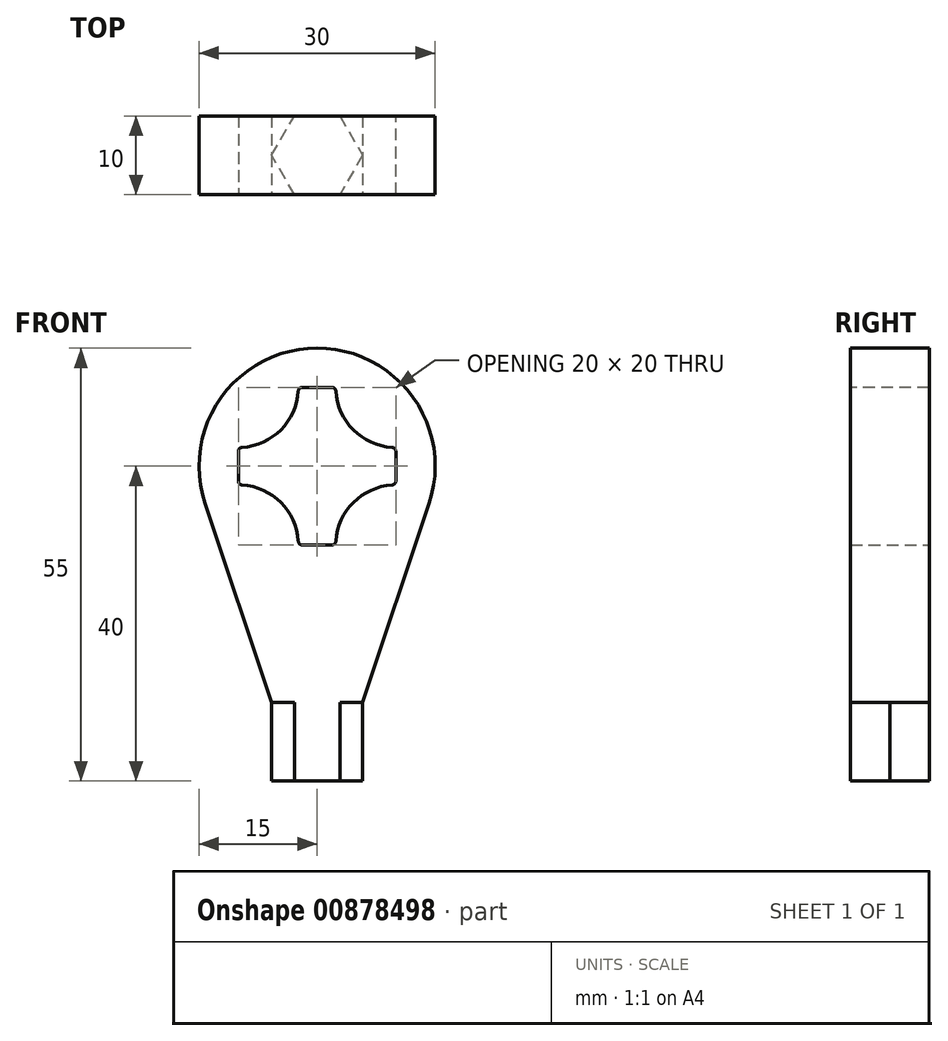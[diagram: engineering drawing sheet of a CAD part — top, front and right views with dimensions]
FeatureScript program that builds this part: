
annotation { "Feature Type Name" : "Feature", "Feature Type Description" : "" }
export const myFeature = defineFeature(function(context is Context, id is Id, definition is map)
    precondition{}
    {
        {
            var Q0;
            Q0=qCreatedBy(makeId("Front.planeOp"),FACE);
            var sketch = newSketch(context, id + "F0", { "sketchPlane" : qUnion([Q0])});
            skLineSegment(sketch, "E0.bottom", {"start": v(10, 10) * mm, "end": v(-10, 10) * mm});
            skLineSegment(sketch, "E0.top", {"start": v(10, -10) * mm, "end": v(-10, -10) * mm});
            skLineSegment(sketch, "E0.left", {"start": v(10, 10) * mm, "end": v(10, -10) * mm});
            skLineSegment(sketch, "E0.right", {"start": v(-10, 10) * mm, "end": v(-10, -10) * mm});
            skPoint(sketch, "E0.middle", {"position": v(0, 0) * mm});
            skCircle(sketch, "E1", {"center": v(0, 0) * mm, "radius": 15 * mm});
            skLineSegment(sketch, "E2", {"start": v(-2.38, 10) * mm, "end": v(2.37, 10) * mm});
            skPoint(sketch, "E3", {"position": v(0, 10) * mm});
            skLineSegment(sketch, "E4", {"start": v(-10, 2.38) * mm, "end": v(-10, -2.38) * mm});
            skLineSegment(sketch, "E5", {"start": v(10, 2.37) * mm, "end": v(10, -2.38) * mm});
            skLineSegment(sketch, "E6", {"start": v(-2.37, -10) * mm, "end": v(2.38, -10) * mm});
            skPoint(sketch, "E7", {"position": v(-10, 0) * mm});
            skPoint(sketch, "E8", {"position": v(10, 0) * mm});
            skPoint(sketch, "E9", {"position": v(0, -10) * mm});
            skCircle(sketch, "E10", {"center": v(-10, 10) * mm, "radius": 7.63 * mm});
            skCircle(sketch, "E11", {"center": v(10, 10) * mm, "radius": 7.63 * mm});
            skCircle(sketch, "E12", {"center": v(10, -10) * mm, "radius": 7.63 * mm});
            skCircle(sketch, "E13", {"center": v(-10, -10) * mm, "radius": 7.63 * mm});
            skSolve(sketch);
        }
        {
            var Q0;
            {var subQ0=sQuery(id+"F0.wireOp",EDGE,"E13");var subQ1=sQuery(id+"F0.wireOp",EDGE,"E0.right");var subQ2=makeQuery(id+"F0.imprint","INTERSECT",VERTEX,{"derivedFrom":[subQ1,subQ0]});Q0=makeQuery(id+"F0.imprint","IMPRINT",FACE,{"disambiguationData":[TD([[makeQuery(id+"F0.imprint","IMPRINT",EDGE,{"disambiguationData":[TD([[subQ2,1.0]])],"derivedFrom":subQ1}),-1.0]])]});}
            var Q1;
            {var subQ1=sQuery(id+"F0.wireOp",EDGE,"E0.bottom");var subQ3=sQuery(id+"F0.wireOp",EDGE,"E10");var subQ5=makeQuery(id+"F0.imprint","INTERSECT",VERTEX,{"derivedFrom":[subQ1,subQ3]});Q1=makeQuery(id+"F0.imprint","IMPRINT",FACE,{"disambiguationData":[TD([[makeQuery(id+"F0.imprint","IMPRINT",EDGE,{"disambiguationData":[TD([[subQ5,-1.0]])],"derivedFrom":subQ1}),-1.0]])]});}
            var Q2;
            {var subQ0=sQuery(id+"F0.wireOp",EDGE,"E10");var subQ1=sQuery(id+"F0.wireOp",EDGE,"E0.bottom");var subQ2=makeQuery(id+"F0.imprint","INTERSECT",VERTEX,{"derivedFrom":[subQ1,subQ0]});Q2=makeQuery(id+"F0.imprint","IMPRINT",FACE,{"disambiguationData":[TD([[makeQuery(id+"F0.imprint","IMPRINT",EDGE,{"disambiguationData":[TD([[subQ2,-1.0]])],"derivedFrom":subQ1}),1.0]])]});}
            var Q3;
            {var subQ0=sQuery(id+"F0.wireOp",EDGE,"E10");var subQ1=sQuery(id+"F0.wireOp",EDGE,"E0.bottom");var subQ2=makeQuery(id+"F0.imprint","INTERSECT",VERTEX,{"derivedFrom":[subQ1,subQ0]});Q3=makeQuery(id+"F0.imprint","IMPRINT",FACE,{"disambiguationData":[TD([[makeQuery(id+"F0.imprint","IMPRINT",EDGE,{"disambiguationData":[TD([[subQ2,1.0]])],"derivedFrom":subQ1}),-1.0]])]});}
            var Q4;
            {var subQ3=sQuery(id+"F0.wireOp",EDGE,"E0.left");var subQ6=sQuery(id+"F0.wireOp",EDGE,"E0.bottom");var subQ7=makeQuery(id+"F0.imprint","INTERSECT",VERTEX,{"derivedFrom":[subQ6,subQ3]});Q4=makeQuery(id+"F0.imprint","IMPRINT",FACE,{"disambiguationData":[TD([[makeQuery(id+"F0.imprint","IMPRINT",EDGE,{"disambiguationData":[TD([[subQ7,-1.0]])],"derivedFrom":subQ6}),-1.0]])]});}
            var Q5;
            {var subQ0=sQuery(id+"F0.wireOp",EDGE,"E12");var subQ1=sQuery(id+"F0.wireOp",EDGE,"E0.left");var subQ2=makeQuery(id+"F0.imprint","INTERSECT",VERTEX,{"derivedFrom":[subQ1,subQ0]});Q5=makeQuery(id+"F0.imprint","IMPRINT",FACE,{"disambiguationData":[TD([[makeQuery(id+"F0.imprint","IMPRINT",EDGE,{"disambiguationData":[TD([[subQ2,1.0]])],"derivedFrom":subQ1}),1.0]])]});}
            var Q6;
            {var subQ1=sQuery(id+"F0.wireOp",EDGE,"E0.left");var subQ6=sQuery(id+"F0.wireOp",EDGE,"E0.top");var subQ7=makeQuery(id+"F0.imprint","INTERSECT",VERTEX,{"derivedFrom":[subQ6,subQ1]});Q6=makeQuery(id+"F0.imprint","IMPRINT",FACE,{"disambiguationData":[TD([[makeQuery(id+"F0.imprint","IMPRINT",EDGE,{"disambiguationData":[TD([[subQ7,-1.0]])],"derivedFrom":subQ6}),1.0]])]});}
            var Q7;
            {var subQ0=sQuery(id+"F0.wireOp",EDGE,"E13");var subQ1=sQuery(id+"F0.wireOp",EDGE,"E0.top");var subQ2=makeQuery(id+"F0.imprint","INTERSECT",VERTEX,{"derivedFrom":[subQ1,subQ0]});Q7=makeQuery(id+"F0.imprint","IMPRINT",FACE,{"disambiguationData":[TD([[makeQuery(id+"F0.imprint","IMPRINT",EDGE,{"disambiguationData":[TD([[subQ2,1.0]])],"derivedFrom":subQ1}),1.0]])]});}
            var Q8;
            {var subQ0=sQuery(id+"F0.wireOp",EDGE,"E13");var subQ1=sQuery(id+"F0.wireOp",EDGE,"E0.top");var subQ2=makeQuery(id+"F0.imprint","INTERSECT",VERTEX,{"derivedFrom":[subQ1,subQ0]});Q8=makeQuery(id+"F0.imprint","IMPRINT",FACE,{"disambiguationData":[TD([[makeQuery(id+"F0.imprint","IMPRINT",EDGE,{"disambiguationData":[TD([[subQ2,-1.0]])],"derivedFrom":subQ1}),1.0]])]});}
            var Q9;
            {var subQ0=sQuery(id+"F0.wireOp",EDGE,"E13");var subQ1=sQuery(id+"F0.wireOp",EDGE,"E0.top");var subQ2=makeQuery(id+"F0.imprint","INTERSECT",VERTEX,{"derivedFrom":[subQ1,subQ0]});Q9=makeQuery(id+"F0.imprint","IMPRINT",FACE,{"disambiguationData":[TD([[makeQuery(id+"F0.imprint","IMPRINT",EDGE,{"disambiguationData":[TD([[subQ2,-1.0]])],"derivedFrom":subQ1}),-1.0]])]});}
            var Q10;
            {var subQ0=sQuery(id+"F0.wireOp",EDGE,"E0.left");var subQ1=sQuery(id+"F0.wireOp",EDGE,"E0.top");var subQ2=makeQuery(id+"F0.imprint","INTERSECT",VERTEX,{"derivedFrom":[subQ1,subQ0]});Q10=makeQuery(id+"F0.imprint","IMPRINT",FACE,{"disambiguationData":[TD([[makeQuery(id+"F0.imprint","IMPRINT",EDGE,{"disambiguationData":[TD([[subQ2,-1.0]])],"derivedFrom":subQ1}),-1.0]])]});}
            var Q11;
            {var subQ0=sQuery(id+"F0.wireOp",EDGE,"E0.left");var subQ1=sQuery(id+"F0.wireOp",EDGE,"E0.bottom");var subQ2=makeQuery(id+"F0.imprint","INTERSECT",VERTEX,{"derivedFrom":[subQ1,subQ0]});Q11=makeQuery(id+"F0.imprint","IMPRINT",FACE,{"disambiguationData":[TD([[makeQuery(id+"F0.imprint","IMPRINT",EDGE,{"disambiguationData":[TD([[subQ2,-1.0]])],"derivedFrom":subQ1}),1.0]])]});}
            extrude(context, id + "F1", {"entities" : qUnion([Q0, Q1, Q2, Q3, Q4, Q5, Q6, Q7, Q8, Q9, Q10, Q11]), "depth" : 3 * mm, "offsetDistance" : 25 * mm});
        }
        {
            var Q0;
            Q0=makeQuery(id+"F1.opExtrude","CAP_FACE",FACE,{"disambiguationData":[OSD([sQuery(id+"F0.wireOp",EDGE,"E0.bottom"),sQuery(id+"F0.wireOp",EDGE,"E0.top"),sQuery(id+"F0.wireOp",EDGE,"E0.left"),sQuery(id+"F0.wireOp",EDGE,"E0.right"),sQuery(id+"F0.wireOp",EDGE,"E1"),sQuery(id+"F0.wireOp",EDGE,"E10"),sQuery(id+"F0.wireOp",EDGE,"E11"),sQuery(id+"F0.wireOp",EDGE,"E12"),sQuery(id+"F0.wireOp",EDGE,"E13")])],"isStart":false});
            var sketch = newSketch(context, id + "F2", { "sketchPlane" : qUnion([Q0])});
            skLineSegment(sketch, "E14", {"start": v(-15, 0) * mm, "end": v(-15, -40) * mm});
            skLineSegment(sketch, "E15", {"start": v(-15, -40) * mm, "end": v(15, -40) * mm});
            skLineSegment(sketch, "E16", {"start": v(15, -40) * mm, "end": v(15, 0) * mm});
            skSolve(sketch);
        }
        {
            var Q0;
            Q0=qCreatedBy(makeId("Top.planeOp"),FACE);
            cPlane(context, id + "F3", {"entities" : qUnion([Q0]), "cplaneType" : CPlaneType.OFFSET, "offset" : 40 * mm, "oppositeDirection" : true, "width" : 150 * mm, "height" : 150 * mm});
        }
        {
            var Q0;
            Q0=qCreatedBy(id+"F3.planeOp",FACE);
            var sketch = newSketch(context, id + "F4", { "sketchPlane" : qUnion([Q0])});
            skLineSegment(sketch, "E17", {"start": v(-15, -1.5) * mm, "end": v(15, -1.5) * mm, "construction": true});
            skCircle(sketch, "E18.cCircle", {"center": v(0, -1.5) * mm, "radius": 5 * mm, "construction": true});
            skLineSegment(sketch, "E18.0", {"start": v(-2.89, 3.5) * mm, "end": v(2.89, 3.5) * mm});
            skLineSegment(sketch, "E18.1", {"start": v(2.89, 3.5) * mm, "end": v(5.77, -1.5) * mm});
            skLineSegment(sketch, "E18.2", {"start": v(5.77, -1.5) * mm, "end": v(2.89, -6.5) * mm});
            skLineSegment(sketch, "E18.3", {"start": v(2.89, -6.5) * mm, "end": v(-2.89, -6.5) * mm});
            skLineSegment(sketch, "E18.4", {"start": v(-2.89, -6.5) * mm, "end": v(-5.77, -1.5) * mm});
            skLineSegment(sketch, "E18.5", {"start": v(-5.77, -1.5) * mm, "end": v(-2.89, 3.5) * mm});
            skPoint(sketch, "E18.0.midPoint", {"position": v(0, 3.5) * mm});
            skLineSegment(sketch, "E19", {"start": v(0, 0) * mm, "end": v(0, -3) * mm});
            skSolve(sketch);
        }
        {
            var Q0;
            Q0=makeQuery(id+"F4.imprint","IMPRINT",FACE,{"disambiguationData":[TD([[makeQuery(id+"F4.imprint","IMPRINT",EDGE,{"derivedFrom":sQuery(id+"F4.wireOp",EDGE,"E18.0")}),-1.0]])]});
            extrude(context, id + "F5", {"entities" : qUnion([Q0]), "depth" : 10 * mm, "offsetDistance" : 25 * mm});
        }
        {
            var Q0;
            Q0=makeQuery(id+"F1.opExtrude","CAP_FACE",FACE,{"disambiguationData":[OSD([sQuery(id+"F0.wireOp",EDGE,"E0.bottom"),sQuery(id+"F0.wireOp",EDGE,"E0.top"),sQuery(id+"F0.wireOp",EDGE,"E0.left"),sQuery(id+"F0.wireOp",EDGE,"E0.right"),sQuery(id+"F0.wireOp",EDGE,"E1"),sQuery(id+"F0.wireOp",EDGE,"E10"),sQuery(id+"F0.wireOp",EDGE,"E11"),sQuery(id+"F0.wireOp",EDGE,"E12"),sQuery(id+"F0.wireOp",EDGE,"E13")])],"isStart":true});
            var sketch = newSketch(context, id + "F6", { "sketchPlane" : qUnion([Q0])});
            skLineSegment(sketch, "E20", {"start": v(-14.22, -4.76) * mm, "end": v(-5.77, -30) * mm});
            skLineSegment(sketch, "E21", {"start": v(-5.77, -30) * mm, "end": v(5.77, -30) * mm});
            skLineSegment(sketch, "E22", {"start": v(5.77, -30) * mm, "end": v(14.22, -4.76) * mm});
            skArc(sketch, "E23.0", {"start": v(-14.22, -4.76) * mm, "mid": v(0, -15) * mm, "end": v(14.22, -4.76) * mm});
            skSolve(sketch);
        }
        {
            var Q0;
            Q0=makeQuery(id+"F6.imprint","IMPRINT",FACE,{"disambiguationData":[TD([[makeQuery(id+"F6.imprint","IMPRINT",EDGE,{"derivedFrom":sQuery(id+"F6.wireOp",EDGE,"E20")}),1.0]])]});
            var Q1;
            Q1=makeQuery(id+"F1.opExtrude","CAP_FACE",FACE,{"disambiguationData":[OSD([sQuery(id+"F0.wireOp",EDGE,"E0.bottom"),sQuery(id+"F0.wireOp",EDGE,"E0.top"),sQuery(id+"F0.wireOp",EDGE,"E0.left"),sQuery(id+"F0.wireOp",EDGE,"E0.right"),sQuery(id+"F0.wireOp",EDGE,"E1"),sQuery(id+"F0.wireOp",EDGE,"E10"),sQuery(id+"F0.wireOp",EDGE,"E11"),sQuery(id+"F0.wireOp",EDGE,"E12"),sQuery(id+"F0.wireOp",EDGE,"E13")])],"isStart":false});
            extrude(context, id + "F7", {"entities" : qUnion([Q0]), "endBound" : BoundingType.UP_TO_SURFACE, "oppositeDirection" : true, "depth" : 25 * mm, "endBoundEntityFace" : qUnion([Q1]), "offsetDistance" : 25 * mm});
        }
        {
            var Q0;
            Q0=makeQuery(id+"F7.opExtrude","CAP_FACE",FACE,{"disambiguationData":[OSD([sQuery(id+"F6.wireOp",EDGE,"E20"),sQuery(id+"F6.wireOp",EDGE,"E21"),sQuery(id+"F6.wireOp",EDGE,"E22"),sQuery(id+"F6.wireOp",EDGE,"E23.0")])],"isStart":true});
            var Q1;
            Q1=makeQuery(id+"F1.opExtrude","CAP_FACE",FACE,{"disambiguationData":[OSD([sQuery(id+"F0.wireOp",EDGE,"E0.bottom"),sQuery(id+"F0.wireOp",EDGE,"E0.top"),sQuery(id+"F0.wireOp",EDGE,"E0.left"),sQuery(id+"F0.wireOp",EDGE,"E0.right"),sQuery(id+"F0.wireOp",EDGE,"E1"),sQuery(id+"F0.wireOp",EDGE,"E10"),sQuery(id+"F0.wireOp",EDGE,"E11"),sQuery(id+"F0.wireOp",EDGE,"E12"),sQuery(id+"F0.wireOp",EDGE,"E13")])],"isStart":true});
            var Q2;
            Q2=makeQuery(id+"F5.opExtrude","SWEPT_FACE",FACE,{"disambiguationData":[OSD([sQuery(id+"F4.wireOp",EDGE,"E18.0")])]});
            extrude(context, id + "F8", {"entities" : qUnion([Q0, Q1]), "endBound" : BoundingType.UP_TO_SURFACE, "depth" : 25 * mm, "endBoundEntityFace" : qUnion([Q2]), "offsetDistance" : 25 * mm});
        }
        {
            var Q0;
            Q0=makeQuery(id+"F1.opExtrude","CAP_FACE",FACE,{"disambiguationData":[OSD([sQuery(id+"F0.wireOp",EDGE,"E0.bottom"),sQuery(id+"F0.wireOp",EDGE,"E0.top"),sQuery(id+"F0.wireOp",EDGE,"E0.left"),sQuery(id+"F0.wireOp",EDGE,"E0.right"),sQuery(id+"F0.wireOp",EDGE,"E1"),sQuery(id+"F0.wireOp",EDGE,"E10"),sQuery(id+"F0.wireOp",EDGE,"E11"),sQuery(id+"F0.wireOp",EDGE,"E12"),sQuery(id+"F0.wireOp",EDGE,"E13")])],"isStart":false});
            var Q1;
            Q1=makeQuery(id+"F7.opExtrude","CAP_FACE",FACE,{"disambiguationData":[OSD([sQuery(id+"F6.wireOp",EDGE,"E20"),sQuery(id+"F6.wireOp",EDGE,"E21"),sQuery(id+"F6.wireOp",EDGE,"E22"),sQuery(id+"F6.wireOp",EDGE,"E23.0")])],"isStart":false});
            var Q2;
            Q2=makeQuery(id+"F5.opExtrude","SWEPT_FACE",FACE,{"disambiguationData":[OSD([sQuery(id+"F4.wireOp",EDGE,"E18.3")])]});
            extrude(context, id + "F9", {"entities" : qUnion([Q0, Q1]), "endBound" : BoundingType.UP_TO_SURFACE, "depth" : 25 * mm, "endBoundEntityFace" : qUnion([Q2]), "offsetDistance" : 25 * mm});
        }
        {
            var Q0;
            Q0=makeQuery(id+"F5.opExtrude","SWEPT_BODY",BODY,{"disambiguationData":[OSD([sQuery(id+"F4.wireOp",EDGE,"E18.0"),sQuery(id+"F4.wireOp",EDGE,"E18.1"),sQuery(id+"F4.wireOp",EDGE,"E18.2"),sQuery(id+"F4.wireOp",EDGE,"E18.3"),sQuery(id+"F4.wireOp",EDGE,"E18.4"),sQuery(id+"F4.wireOp",EDGE,"E18.5")])]});
            var Q1;
            Q1=makeQuery(id+"F8.opExtrude","SWEPT_BODY",BODY,{"disambiguationData":[OSD([sQuery(id+"F6.wireOp",EDGE,"E20"),sQuery(id+"F6.wireOp",EDGE,"E21"),sQuery(id+"F6.wireOp",EDGE,"E22"),sQuery(id+"F6.wireOp",EDGE,"E23.0")])]});
            var Q2;
            Q2=makeQuery(id+"F7.opExtrude","SWEPT_BODY",BODY,{"disambiguationData":[OSD([sQuery(id+"F6.wireOp",EDGE,"E20"),sQuery(id+"F6.wireOp",EDGE,"E21"),sQuery(id+"F6.wireOp",EDGE,"E22"),sQuery(id+"F6.wireOp",EDGE,"E23.0")])]});
            var Q3;
            Q3=makeQuery(id+"F9.opExtrude","SWEPT_BODY",BODY,{"disambiguationData":[OSD([sQuery(id+"F6.wireOp",EDGE,"E20"),sQuery(id+"F6.wireOp",EDGE,"E21"),sQuery(id+"F6.wireOp",EDGE,"E22"),sQuery(id+"F6.wireOp",EDGE,"E23.0")])]});
            var Q4;
            Q4=makeQuery(id+"F8.opExtrude","SWEPT_BODY",BODY,{"disambiguationData":[OSD([sQuery(id+"F0.wireOp",EDGE,"E0.bottom"),sQuery(id+"F0.wireOp",EDGE,"E0.top"),sQuery(id+"F0.wireOp",EDGE,"E0.left"),sQuery(id+"F0.wireOp",EDGE,"E0.right"),sQuery(id+"F0.wireOp",EDGE,"E1"),sQuery(id+"F0.wireOp",EDGE,"E10"),sQuery(id+"F0.wireOp",EDGE,"E11"),sQuery(id+"F0.wireOp",EDGE,"E12"),sQuery(id+"F0.wireOp",EDGE,"E13")])]});
            var Q5;
            Q5=makeQuery(id+"F1.opExtrude","SWEPT_BODY",BODY,{"disambiguationData":[OSD([sQuery(id+"F0.wireOp",EDGE,"E0.bottom"),sQuery(id+"F0.wireOp",EDGE,"E0.top"),sQuery(id+"F0.wireOp",EDGE,"E0.left"),sQuery(id+"F0.wireOp",EDGE,"E0.right"),sQuery(id+"F0.wireOp",EDGE,"E1"),sQuery(id+"F0.wireOp",EDGE,"E10"),sQuery(id+"F0.wireOp",EDGE,"E11"),sQuery(id+"F0.wireOp",EDGE,"E12"),sQuery(id+"F0.wireOp",EDGE,"E13")])]});
            var Q6;
            Q6=makeQuery(id+"F9.opExtrude","SWEPT_BODY",BODY,{"disambiguationData":[OSD([sQuery(id+"F0.wireOp",EDGE,"E0.bottom"),sQuery(id+"F0.wireOp",EDGE,"E0.top"),sQuery(id+"F0.wireOp",EDGE,"E0.left"),sQuery(id+"F0.wireOp",EDGE,"E0.right"),sQuery(id+"F0.wireOp",EDGE,"E1"),sQuery(id+"F0.wireOp",EDGE,"E10"),sQuery(id+"F0.wireOp",EDGE,"E11"),sQuery(id+"F0.wireOp",EDGE,"E12"),sQuery(id+"F0.wireOp",EDGE,"E13")])]});
            booleanBodies(context, id + "F10", {"operationType" : BooleanOperationType.UNION, "tools" : qUnion([Q0, Q1, Q2, Q3, Q4, Q5, Q6])});
        }
        {
            var Q0;
            {var subQ0=sQuery(id+"F0.wireOp",EDGE,"E12");var subQ1=sQuery(id+"F0.wireOp",EDGE,"E0.left");Q0=makeQuery(id+"F10.opBoolean","MERGE",EDGE,{"derivedFrom":[makeQuery(id+"F1.opExtrude","SWEPT_EDGE",EDGE,{"disambiguationData":[OSD([subQ1,subQ0])]}),makeQuery(id+"F8.opExtrude","SWEPT_EDGE",EDGE,{"disambiguationData":[OSD([subQ1,subQ0])]}),makeQuery(id+"F9.opExtrude","SWEPT_EDGE",EDGE,{"disambiguationData":[OSD([subQ1,subQ0])]})]});}
            var Q1;
            {var subQ0=sQuery(id+"F0.wireOp",EDGE,"E11");var subQ1=sQuery(id+"F0.wireOp",EDGE,"E0.left");Q1=makeQuery(id+"F10.opBoolean","MERGE",EDGE,{"derivedFrom":[makeQuery(id+"F1.opExtrude","SWEPT_EDGE",EDGE,{"disambiguationData":[OSD([subQ1,subQ0])]}),makeQuery(id+"F8.opExtrude","SWEPT_EDGE",EDGE,{"disambiguationData":[OSD([subQ1,subQ0])]}),makeQuery(id+"F9.opExtrude","SWEPT_EDGE",EDGE,{"disambiguationData":[OSD([subQ1,subQ0])]})]});}
            var Q2;
            {var subQ0=sQuery(id+"F0.wireOp",EDGE,"E12");var subQ1=sQuery(id+"F0.wireOp",EDGE,"E0.top");Q2=makeQuery(id+"F10.opBoolean","MERGE",EDGE,{"derivedFrom":[makeQuery(id+"F1.opExtrude","SWEPT_EDGE",EDGE,{"disambiguationData":[OSD([subQ1,subQ0])]}),makeQuery(id+"F8.opExtrude","SWEPT_EDGE",EDGE,{"disambiguationData":[OSD([subQ1,subQ0])]}),makeQuery(id+"F9.opExtrude","SWEPT_EDGE",EDGE,{"disambiguationData":[OSD([subQ1,subQ0])]})]});}
            var Q3;
            {var subQ0=sQuery(id+"F0.wireOp",EDGE,"E13");var subQ1=sQuery(id+"F0.wireOp",EDGE,"E0.top");Q3=makeQuery(id+"F10.opBoolean","MERGE",EDGE,{"derivedFrom":[makeQuery(id+"F1.opExtrude","SWEPT_EDGE",EDGE,{"disambiguationData":[OSD([subQ1,subQ0])]}),makeQuery(id+"F8.opExtrude","SWEPT_EDGE",EDGE,{"disambiguationData":[OSD([subQ1,subQ0])]}),makeQuery(id+"F9.opExtrude","SWEPT_EDGE",EDGE,{"disambiguationData":[OSD([subQ1,subQ0])]})]});}
            var Q4;
            {var subQ0=sQuery(id+"F0.wireOp",EDGE,"E13");var subQ1=sQuery(id+"F0.wireOp",EDGE,"E0.right");Q4=makeQuery(id+"F10.opBoolean","MERGE",EDGE,{"derivedFrom":[makeQuery(id+"F1.opExtrude","SWEPT_EDGE",EDGE,{"disambiguationData":[OSD([subQ1,subQ0])]}),makeQuery(id+"F8.opExtrude","SWEPT_EDGE",EDGE,{"disambiguationData":[OSD([subQ1,subQ0])]}),makeQuery(id+"F9.opExtrude","SWEPT_EDGE",EDGE,{"disambiguationData":[OSD([subQ1,subQ0])]})]});}
            var Q5;
            {var subQ0=sQuery(id+"F0.wireOp",EDGE,"E10");var subQ1=sQuery(id+"F0.wireOp",EDGE,"E0.right");Q5=makeQuery(id+"F10.opBoolean","MERGE",EDGE,{"derivedFrom":[makeQuery(id+"F1.opExtrude","SWEPT_EDGE",EDGE,{"disambiguationData":[OSD([subQ1,subQ0])]}),makeQuery(id+"F8.opExtrude","SWEPT_EDGE",EDGE,{"disambiguationData":[OSD([subQ1,subQ0])]}),makeQuery(id+"F9.opExtrude","SWEPT_EDGE",EDGE,{"disambiguationData":[OSD([subQ1,subQ0])]})]});}
            var Q6;
            {var subQ0=sQuery(id+"F0.wireOp",EDGE,"E10");var subQ1=sQuery(id+"F0.wireOp",EDGE,"E0.bottom");Q6=makeQuery(id+"F10.opBoolean","MERGE",EDGE,{"derivedFrom":[makeQuery(id+"F1.opExtrude","SWEPT_EDGE",EDGE,{"disambiguationData":[OSD([subQ1,subQ0])]}),makeQuery(id+"F8.opExtrude","SWEPT_EDGE",EDGE,{"disambiguationData":[OSD([subQ1,subQ0])]}),makeQuery(id+"F9.opExtrude","SWEPT_EDGE",EDGE,{"disambiguationData":[OSD([subQ1,subQ0])]})]});}
            var Q7;
            {var subQ0=sQuery(id+"F0.wireOp",EDGE,"E11");var subQ1=sQuery(id+"F0.wireOp",EDGE,"E0.bottom");Q7=makeQuery(id+"F10.opBoolean","MERGE",EDGE,{"derivedFrom":[makeQuery(id+"F1.opExtrude","SWEPT_EDGE",EDGE,{"disambiguationData":[OSD([subQ1,subQ0])]}),makeQuery(id+"F8.opExtrude","SWEPT_EDGE",EDGE,{"disambiguationData":[OSD([subQ1,subQ0])]}),makeQuery(id+"F9.opExtrude","SWEPT_EDGE",EDGE,{"disambiguationData":[OSD([subQ1,subQ0])]})]});}
            fillet(context, id + "F11", {"entities" : qUnion([Q0, Q1, Q2, Q3, Q4, Q5, Q6, Q7]), "radius" : .5 * mm, "tangentPropagation" : true, "allowEdgeOverflow" : false});
        }
    });
